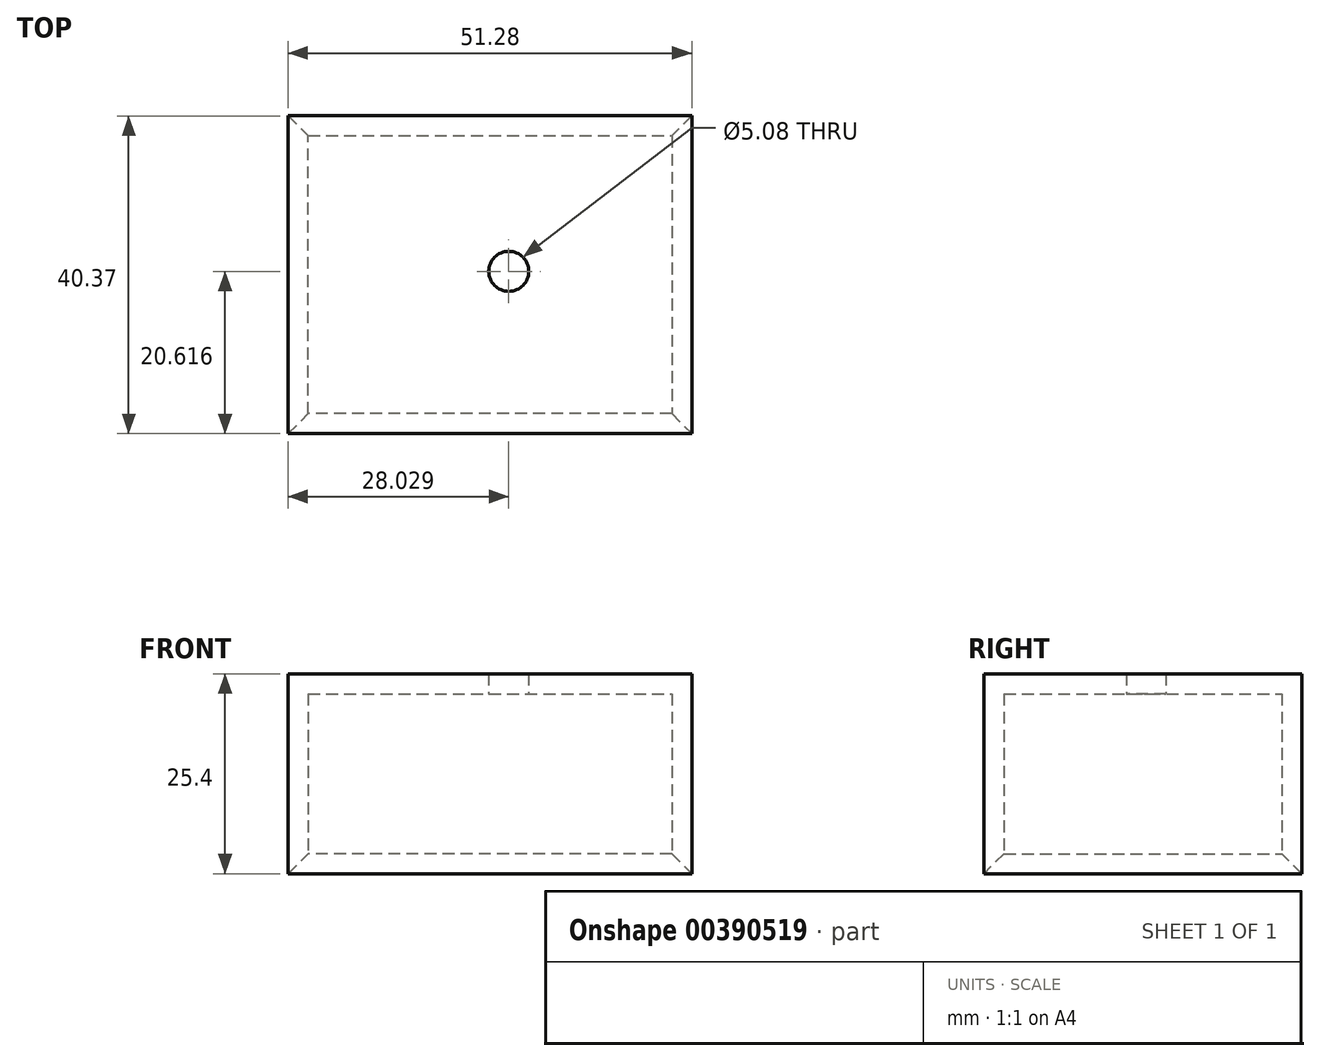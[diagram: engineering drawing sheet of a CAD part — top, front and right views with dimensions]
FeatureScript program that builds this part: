
annotation { "Feature Type Name" : "Feature", "Feature Type Description" : "" }
export const myFeature = defineFeature(function(context is Context, id is Id, definition is map)
    precondition{}
    {
        {
            var Q0;
            Q0=qCreatedBy(makeId("Top.planeOp"),FACE);
            var sketch = newSketch(context, id + "F0", { "sketchPlane" : qUnion([Q0])});
            skLineSegment(sketch, "E0.bottom", {"start": v(0, 0) * mm, "end": v(51.28, 0) * mm});
            skLineSegment(sketch, "E0.top", {"start": v(0, 40.37) * mm, "end": v(51.28, 40.37) * mm});
            skLineSegment(sketch, "E0.left", {"start": v(0, 0) * mm, "end": v(0, 40.37) * mm});
            skLineSegment(sketch, "E0.right", {"start": v(51.28, 0) * mm, "end": v(51.28, 40.37) * mm});
            skSolve(sketch);
        }
        {
            var Q0;
            Q0 = qSketchRegion(id + "F0", true);
            var Q1;
            Q1=makeQuery(id+"F0.imprint","IMPRINT",FACE,{"disambiguationData":[TD([[makeQuery(id+"F0.imprint","IMPRINT",EDGE,{"derivedFrom":sQuery(id+"F0.wireOp",EDGE,"E0.bottom")}),1.0]])]});
            extrude(context, id + "F1", {"entities" : qUnion([Q0, Q1]), "depth" : 25.4 * mm});
        }
        {
            var Q0;
            Q0=makeQuery(id+"F1.opExtrude","CAP_FACE",FACE,{"disambiguationData":[OSD([sQuery(id+"F0.wireOp",EDGE,"E0.bottom"),sQuery(id+"F0.wireOp",EDGE,"E0.top"),sQuery(id+"F0.wireOp",EDGE,"E0.left"),sQuery(id+"F0.wireOp",EDGE,"E0.right")])],"isStart":false});
            var sketch = newSketch(context, id + "F2", { "sketchPlane" : qUnion([Q0])});
            skLineSegment(sketch, "E1.bottom", {"start": v(26.4, 12.7) * mm, "end": v(12.22, 12.7) * mm});
            skLineSegment(sketch, "E1.top", {"start": v(26.4, 28.48) * mm, "end": v(12.22, 28.48) * mm});
            skLineSegment(sketch, "E1.left", {"start": v(26.4, 12.7) * mm, "end": v(26.4, 28.48) * mm});
            skLineSegment(sketch, "E1.right", {"start": v(12.22, 12.7) * mm, "end": v(12.22, 28.48) * mm});
            skSolve(sketch);
        }
        {
            var Q0;
            Q0 = qSketchRegion(id + "F2", true);
            var Q1;
            Q1=makeQuery(id+"F2.imprint","IMPRINT",FACE,{"disambiguationData":[TD([[makeQuery(id+"F2.imprint","IMPRINT",EDGE,{"derivedFrom":sQuery(id+"F2.wireOp",EDGE,"E1.bottom")}),-1.0]])]});
            extrude(context, id + "F3", {"entities" : qUnion([Q0, Q1]), "operationType" : NewBodyOperationType.ADD, "oppositeDirection" : true, "depth" : 12.7 * mm});
        }
        {
            var Q0;
            Q0=makeQuery(id+"F1.opExtrude","CAP_FACE",FACE,{"disambiguationData":[OSD([sQuery(id+"F0.wireOp",EDGE,"E0.bottom"),sQuery(id+"F0.wireOp",EDGE,"E0.top"),sQuery(id+"F0.wireOp",EDGE,"E0.left"),sQuery(id+"F0.wireOp",EDGE,"E0.right")])],"isStart":true});
            shell(context, id + "F4", {"entities" : qUnion([Q0]), "thickness" : 2.54 * mm});
        }
        {
            var Q0;
            {var subQ0=sQuery(id+"F0.wireOp",EDGE,"E0.left");Q0=makeQuery(id+"F4.opShell","OFFSET_EDGE",EDGE,{"disambiguationData":[OSD([subQ0]),TDD([makeQuery(id+"F1.opExtrude","CAP_EDGE",EDGE,{"disambiguationData":[OSD([subQ0])],"isStart":true})])]});}
            var Q1;
            {var subQ0=sQuery(id+"F0.wireOp",EDGE,"E0.top");Q1=makeQuery(id+"F4.opShell","OFFSET_EDGE",EDGE,{"disambiguationData":[OSD([subQ0]),TDD([makeQuery(id+"F1.opExtrude","CAP_EDGE",EDGE,{"disambiguationData":[OSD([subQ0])],"isStart":true})])]});}
            var Q2;
            {var subQ0=sQuery(id+"F0.wireOp",EDGE,"E0.right");Q2=makeQuery(id+"F4.opShell","OFFSET_EDGE",EDGE,{"disambiguationData":[OSD([subQ0]),TDD([makeQuery(id+"F1.opExtrude","CAP_EDGE",EDGE,{"disambiguationData":[OSD([subQ0])],"isStart":true})])]});}
            var Q3;
            {var subQ0=sQuery(id+"F0.wireOp",EDGE,"E0.bottom");Q3=makeQuery(id+"F4.opShell","OFFSET_EDGE",EDGE,{"disambiguationData":[OSD([subQ0]),TDD([makeQuery(id+"F1.opExtrude","CAP_EDGE",EDGE,{"disambiguationData":[OSD([subQ0])],"isStart":true})])]});}
            chamfer(context, id + "F5", {"entities" : qUnion([Q0, Q1, Q2, Q3]), "width" : 2.54 * mm, "tangentPropagation" : true});
        }
        {
            var Q0;
            Q0=makeQuery(id+"F4.opShell","OFFSET_FACE",FACE,{"disambiguationData":[OSD([sQuery(id+"F0.wireOp",EDGE,"E0.bottom"),sQuery(id+"F0.wireOp",EDGE,"E0.top"),sQuery(id+"F0.wireOp",EDGE,"E0.left"),sQuery(id+"F0.wireOp",EDGE,"E0.right")])]});
            var sketch = newSketch(context, id + "F6", { "sketchPlane" : qUnion([Q0])});
            skCircle(sketch, "E2", {"center": v(28.03, -20.62) * mm, "radius": 6.07 * mm});
            skSolve(sketch);
        }
        {
            var Q0;
            Q0=sQuery(id+"F6.wireOp",VERTEX,"E2.center");
            var Q1;
            Q1=makeQuery(id+"F1.opExtrude","SWEPT_BODY",BODY,{"disambiguationData":[OSD([sQuery(id+"F0.wireOp",EDGE,"E0.bottom"),sQuery(id+"F0.wireOp",EDGE,"E0.top"),sQuery(id+"F0.wireOp",EDGE,"E0.left"),sQuery(id+"F0.wireOp",EDGE,"E0.right")])]});
            hole(context, id + "F7", {"style" : HoleStyle.C_BORE, "endStyle" : HoleEndStyle.THROUGH, "holeDiameter" : 2.54 * mm, "cBoreDiameter" : 5.08 * mm, "cBoreDepth" : 2.54 * mm, "isTappedThrough" : true, "tappedDepth" : 12.7 * mm, "tapClearance" : 3, "locations" : qUnion([Q0]), "scope" : qUnion([Q1])});
        }
    });
